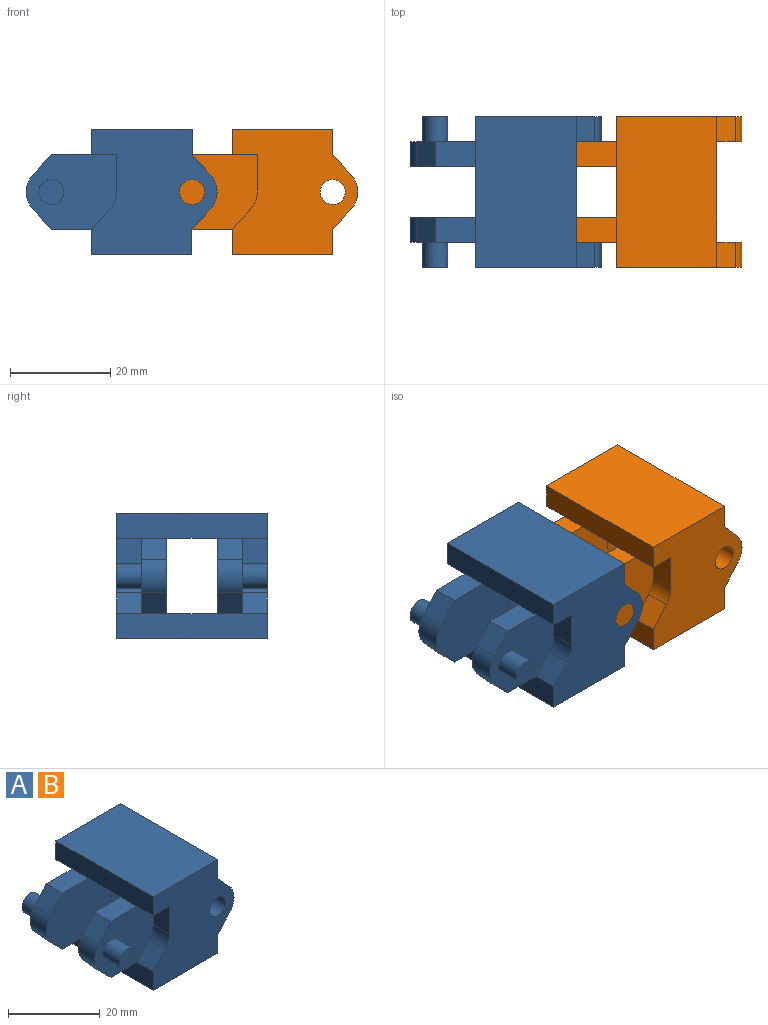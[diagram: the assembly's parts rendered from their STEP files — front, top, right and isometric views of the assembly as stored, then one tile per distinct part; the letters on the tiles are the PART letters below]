
ASSEMBLY  parts=2 mates=1
PART A: 52 faces, bbox 38x30x25 mm
  f0: plane 18x15mm, normal (0,-1,0), area 207.2mm2, adj f2,f3,f4,f6,f13,f15,f20,f24
  f1: plane 5x4.17mm, normal (-0.75,0,0.67), area 28mm2, adj f7,f8,f16,f26
  f2: plane 5x4.17mm, normal (0.75,0,-0.67), area 28mm2, adj f0,f3,f8,f17
  f3: cylinder r=5mm len=6.67mm, axis (0,1,0), area 36.5mm2, adj f0,f2,f4,f8
  f4: plane 5x4.17mm, normal (0.75,0,0.67), area 28mm2, adj f0,f3,f8,f11
  f5: plane 7.5x5mm, normal (-1,0,0), area 37.5mm2, adj f7,f8,f9,f26
  f6: cylinder r=2.5mm len=5mm, axis (0,1,0), area 78.5mm2, adj f0,f8
  f7: cylinder r=5mm len=5mm, axis (0,1,0), area 18.2mm2, adj f1,f5,f8,f26
  f8: plane 25x25mm, normal (0,1,0), area 466mm2, adj f1,f2,f3,f4,f5,f6,f7,f9
  f9: plane 5x5mm, normal (0,0,-1), area 25mm2, adj f5,f8,f10,f26
  f10: plane 30x5mm, normal (-1,0,0), area 150mm2, adj f8,f9,f12,f13,f14,f38,f40,f41
  f11: plane 30x5mm, normal (1,0,0), area 150mm2, adj f4,f8,f12,f13,f34,f38
  f12: plane 30x20mm, normal (0,0,1), area 600mm2, adj f8,f10,f11,f38
  f13: plane 20x20mm, normal (0,0,-1), area 330mm2, adj f0,f10,f11,f24,f27,f30,f47,f49
  f14: plane 8x5mm, normal (0,0,1), area 40mm2, adj f10,f23,f26,f27
  f15: plane 20x20mm, normal (0,0,1), area 280mm2, adj f0,f16,f17,f20,f27,f30,f43,f49
  f16: plane 30x5mm, normal (-1,0,0), area 150mm2, adj f1,f8,f15,f18,f19,f31,f38,f42
  f17: plane 30x5mm, normal (1,0,0), area 150mm2, adj f2,f8,f15,f18,f32,f38
  f18: plane 30x20mm, normal (0,0,-1), area 600mm2, adj f8,f16,f17,f38
  f19: plane 8x5mm, normal (0,0,-1), area 40mm2, adj f16,f21,f26,f27
  f20: plane 5x4.17mm, normal (0.75,0,0.67), area 28mm2, adj f0,f15,f25,f27
  f21: plane 5x4.17mm, normal (-0.75,0,-0.67), area 28mm2, adj f19,f22,f26,f27
  f22: cylinder r=5mm len=6.67mm, axis (0,-1,0), area 36.5mm2, adj f21,f23,f26,f27
  f23: plane 5x4.17mm, normal (-0.75,0,0.67), area 28mm2, adj f14,f22,f26,f27
  f24: plane 7.5x5mm, normal (1,0,0), area 37.5mm2, adj f0,f13,f25,f27
  f25: cylinder r=5mm len=5mm, axis (0,-1,0), area 18.2mm2, adj f0,f20,f24,f27
  f26: plane 18x15mm, normal (0,1,0), area 207.2mm2, adj f1,f5,f7,f9,f14,f19,f21,f22
  f27: plane 25x15mm, normal (0,-1,0), area 285.6mm2, adj f13,f14,f15,f19,f20,f21,f22,f23
  f28: cylinder r=2.5mm len=5mm, axis (0,1,0), area 78.5mm2, adj f26,f29
  f29: plane 5x5mm, normal (0,1,0), area 19.6mm2, adj f28
  f30: plane 18x15mm, normal (0,1,0), area 207.2mm2, adj f13,f15,f32,f33,f34,f36,f43,f47
  f31: plane 5x4.17mm, normal (-0.75,0,0.67), area 28mm2, adj f16,f37,f38,f39
  f32: plane 5x4.17mm, normal (0.75,0,-0.67), area 28mm2, adj f17,f30,f33,f38
  f33: cylinder r=5mm len=6.67mm, axis (0,-1,0), area 36.5mm2, adj f30,f32,f34,f38
  f34: plane 5x4.17mm, normal (0.75,0,0.67), area 28mm2, adj f11,f30,f33,f38
  f35: plane 7.5x5mm, normal (-1,0,0), area 37.5mm2, adj f37,f38,f39,f40
  f36: cylinder r=2.5mm len=5mm, axis (0,-1,0), area 78.5mm2, adj f30,f38
  f37: cylinder r=5mm len=5mm, axis (0,-1,0), area 18.2mm2, adj f31,f35,f38,f39
  f38: plane 25x25mm, normal (0,-1,0), area 466mm2, adj f10,f11,f12,f16,f17,f18,f31,f32
  f39: plane 18x15mm, normal (0,-1,0), area 207.2mm2, adj f31,f35,f37,f40,f41,f42,f44,f45
  f40: plane 5x5mm, normal (0,0,-1), area 25mm2, adj f10,f35,f38,f39
  f41: plane 8x5mm, normal (0,0,1), area 40mm2, adj f10,f39,f46,f49
  f42: plane 8x5mm, normal (0,0,-1), area 40mm2, adj f16,f39,f44,f49
  f43: plane 5x4.17mm, normal (0.75,0,0.67), area 28mm2, adj f15,f30,f48,f49
  f44: plane 5x4.17mm, normal (-0.75,0,-0.67), area 28mm2, adj f39,f42,f45,f49
  f45: cylinder r=5mm len=6.67mm, axis (0,1,0), area 36.5mm2, adj f39,f44,f46,f49
  f46: plane 5x4.17mm, normal (-0.75,0,0.67), area 28mm2, adj f39,f41,f45,f49
  f47: plane 7.5x5mm, normal (1,0,0), area 37.5mm2, adj f13,f30,f48,f49
  f48: cylinder r=5mm len=5mm, axis (0,1,0), area 18.2mm2, adj f30,f43,f47,f49
  f49: plane 25x15mm, normal (0,1,0), area 285.6mm2, adj f13,f15,f41,f42,f43,f44,f45,f46
  f50: cylinder r=2.5mm len=5mm, axis (0,-1,0), area 78.5mm2, adj f39,f51
  f51: plane 5x5mm, normal (0,-1,0), area 19.6mm2, adj f50
PART B: same geometry as A
PLACE A t=(-33.65,7.92,-2.11)mm
PLACE B t=(-5.65,7.92,-2.11)mm
MATE revolute A.f3 <-> B.f22  axis (0,-1,0) through (-13.65,-22.08,5.39)mm
